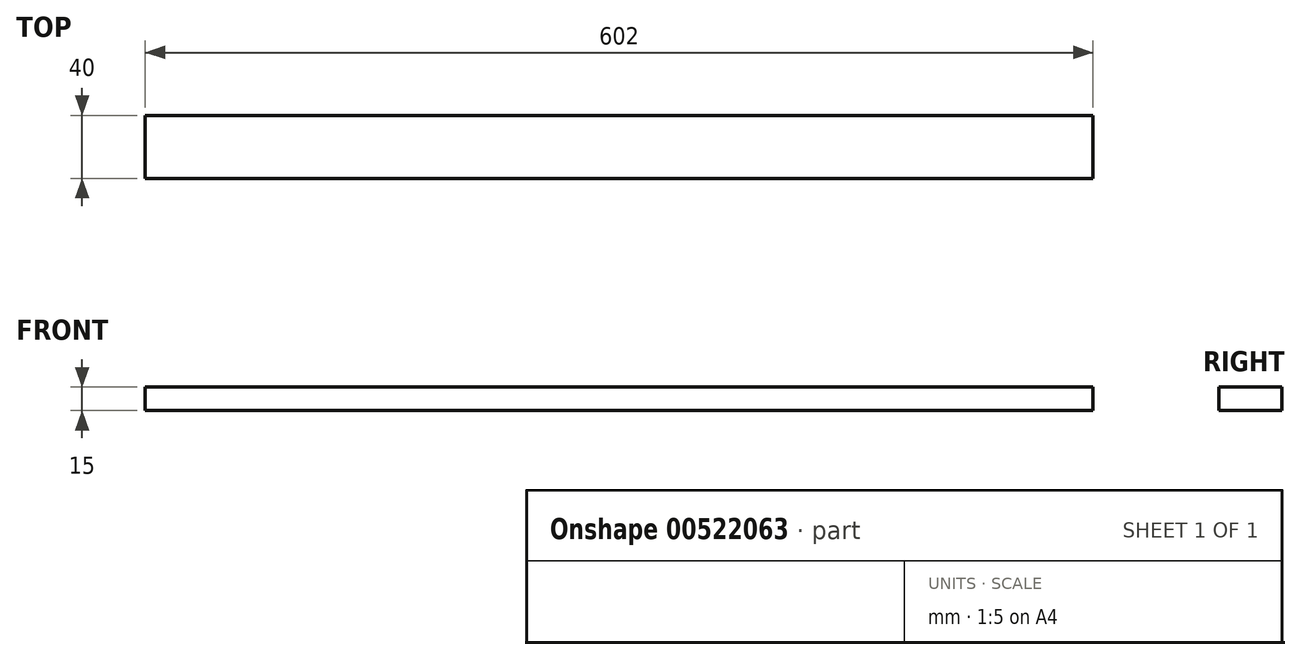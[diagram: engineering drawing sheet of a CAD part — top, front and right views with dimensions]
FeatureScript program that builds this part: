
annotation { "Feature Type Name" : "Feature", "Feature Type Description" : "" }
export const myFeature = defineFeature(function(context is Context, id is Id, definition is map)
    precondition{}
    {
        {
            var Q0;
            Q0=qCreatedBy(makeId("Right.planeOp"),FACE);
            var sketch = newSketch(context, id + "F0", { "sketchPlane" : qUnion([Q0])});
            skLineSegment(sketch, "E0.bottom", {"start": v(0, 0) * mm, "end": v(-40, 0) * mm});
            skLineSegment(sketch, "E0.top", {"start": v(0, 15) * mm, "end": v(-40, 15) * mm});
            skLineSegment(sketch, "E0.left", {"start": v(0, 0) * mm, "end": v(0, 15) * mm});
            skLineSegment(sketch, "E0.right", {"start": v(-40, 0) * mm, "end": v(-40, 15) * mm});
            skSolve(sketch);
        }
        {
            var Q0;
            Q0=makeQuery(id+"F0.imprint","IMPRINT",FACE,{"disambiguationData":[TD([[makeQuery(id+"F0.imprint","IMPRINT",EDGE,{"derivedFrom":sQuery(id+"F0.wireOp",EDGE,"E0.bottom")}),-1.0]])]});
            extrude(context, id + "F1", {"entities" : qUnion([Q0]), "oppositeDirection" : true, "depth" : 602 * mm, "offsetDistance" : 25 * mm});
        }
    });
